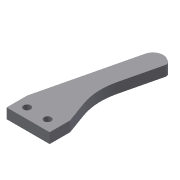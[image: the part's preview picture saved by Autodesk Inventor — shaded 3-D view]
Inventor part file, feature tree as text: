
AUTODESK INVENTOR PART (.ipt)
format: ipt  version: 2018 (Build 220112000, 112)  size: 110,592 bytes
history: native  units: mm
features: extrude x1, sketch x1
ambient origin geometry x8: Origin, YZ Plane, XZ Plane, XY Plane, X Axis, Y Axis, Z Axis, Center Point
bodies: Solid1 (feature_tree)
feature tree (2):
  extrude  "Extrusion1"  Depth=10.0mm
  sketch  "Sketch1"  dims[d0=5.0mm d1=10.0mm d2=3.5mm d3=3.5mm d4=5.0mm d5=11.0mm d6=10.0mm d7=10.0mm d8=10.0mm d9=20.0mm d10=19.198622mm d11=30.0mm d12=10.0mm d13=19.198622mm d14=30.0mm d15=2.0mm d16=5.0mm d17=5.0mm d18=0.0mm]
